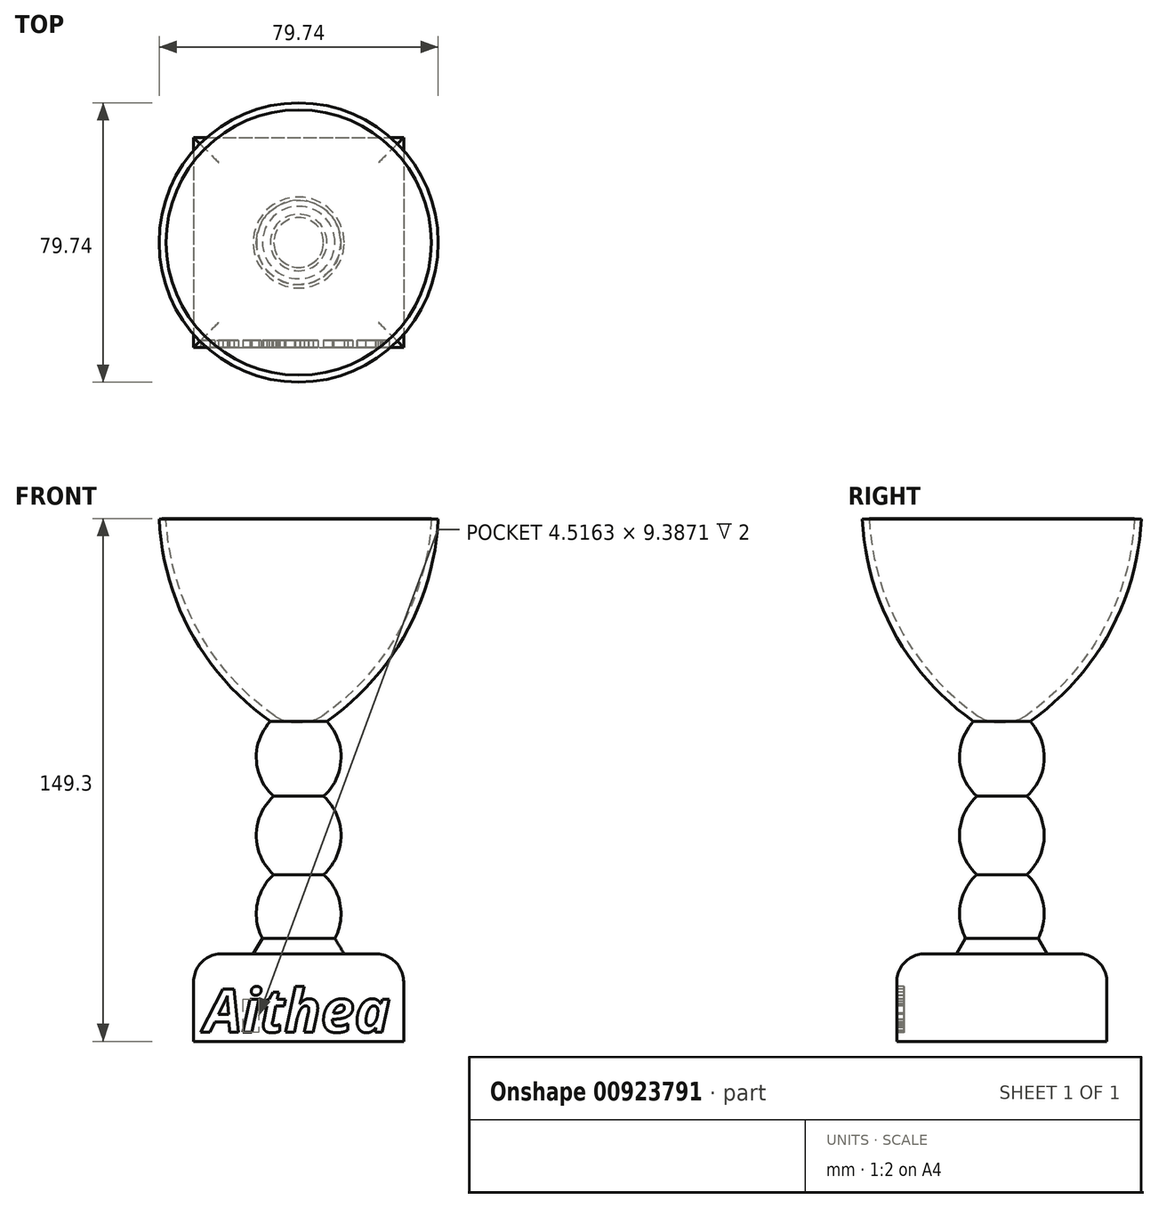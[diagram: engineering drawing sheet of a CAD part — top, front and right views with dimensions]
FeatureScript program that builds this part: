
annotation { "Feature Type Name" : "Feature", "Feature Type Description" : "" }
export const myFeature = defineFeature(function(context is Context, id is Id, definition is map)
    precondition{}
    {
        {
            var Q0;
            Q0=qCreatedBy(makeId("Top.planeOp"),FACE);
            var sketch = newSketch(context, id + "F0", { "sketchPlane" : qUnion([Q0])});
            skLineSegment(sketch, "E0.bottom", {"start": v(0, 0) * mm, "end": v(60, 0) * mm});
            skLineSegment(sketch, "E0.top", {"start": v(0, -60) * mm, "end": v(60, -60) * mm});
            skLineSegment(sketch, "E0.left", {"start": v(0, 0) * mm, "end": v(0, -60) * mm});
            skLineSegment(sketch, "E0.right", {"start": v(60, 0) * mm, "end": v(60, -60) * mm});
            skSolve(sketch);
        }
        {
            var Q0;
            Q0=makeQuery(id+"F0.imprint","IMPRINT",FACE,{"disambiguationData":[TD([[makeQuery(id+"F0.imprint","IMPRINT",EDGE,{"derivedFrom":sQuery(id+"F0.wireOp",EDGE,"E0.bottom")}),-1.0]])]});
            extrude(context, id + "F1", {"entities" : qUnion([Q0]), "depth" : 30 * mm, "offsetDistance" : 25 * mm});
        }
        {
            var Q0;
            Q0=makeQuery(id+"F1.opExtrude","SWEPT_BODY",BODY,{"disambiguationData":[OSD([sQuery(id+"F0.wireOp",EDGE,"E0.bottom"),sQuery(id+"F0.wireOp",EDGE,"E0.top"),sQuery(id+"F0.wireOp",EDGE,"E0.left"),sQuery(id+"F0.wireOp",EDGE,"E0.right")])]});
            transform(context, id + "F2", {"entities" : qUnion([Q0]), "transformType" : TransformType.TRANSLATION_3D, "dx" : -30 * mm, "dy" : 30 * mm, "dz" : 0 * mm, "makeCopy" : false});
        }
        {
            var Q0;
            Q0=qCreatedBy(makeId("Front.planeOp"),FACE);
            var sketch = newSketch(context, id + "F3", { "sketchPlane" : qUnion([Q0])});
            skArc(sketch, "E1", {"start": v(7.1, 30.27) * mm, "mid": v(12.1, 41.45) * mm, "end": v(7.1, 52.63) * mm});
            skArc(sketch, "E2", {"start": v(7.1, 52.63) * mm, "mid": v(12.1, 63.81) * mm, "end": v(7.1, 75) * mm});
            skArc(sketch, "E3", {"start": v(7.1, 75) * mm, "mid": v(12.1, 85.49) * mm, "end": v(8.09, 96.4) * mm});
            skLineSegment(sketch, "E4", {"start": v(0, 30.2) * mm, "end": v(0, 158.08) * mm});
            skLineSegment(sketch, "E5", {"start": v(7.1, 30.27) * mm, "end": v(7.1, 29.78) * mm});
            skLineSegment(sketch, "E6", {"start": v(7.1, 29.78) * mm, "end": v(0, 29.78) * mm});
            skLineSegment(sketch, "E7", {"start": v(0, 29.78) * mm, "end": v(0, 30.2) * mm});
            skArc(sketch, "E8", {"start": v(8.09, 96.4) * mm, "mid": v(30.66, 121.62) * mm, "end": v(39.87, 154.2) * mm});
            skLineSegment(sketch, "E9", {"start": v(37.87, 154.3) * mm, "end": v(39.87, 154.2) * mm});
            skLineSegment(sketch, "E10", {"start": v(0, 96.12) * mm, "end": v(1.06, 96.12) * mm});
            skArc(sketch, "E11.trimOffspring", {"start": v(6.8, 97.93) * mm, "mid": v(28.86, 122.52) * mm, "end": v(37.87, 154.3) * mm});
            skPoint(sketch, "E12.visualSharp", {"position": v(4.09, 96.12) * mm});
            skArc(sketch, "E12.filletArc", {"start": v(1.06, 96.12) * mm, "mid": v(4.07, 96.58) * mm, "end": v(6.8, 97.93) * mm});
            skLineSegment(sketch, "E13", {"start": v(0, 96.12) * mm, "end": v(11.67, 89.78) * mm});
            skSolve(sketch);
        }
        {
            var Q0;
            {var subQ10=sQuery(id+"F3.wireOp",EDGE,"I5DjJ9ts-EXyD-T3Ez-MTNL-TmspGHFE94tQ");Q0=makeQuery(id+"F3.imprint","IMPRINT",FACE,{"disambiguationData":[TD([[makeQuery(id+"F3.imprint","IMPRINT",EDGE,{"derivedFrom":subQ10}),1.0]])]});}
            var Q1;
            {var subQ0=sQuery(id+"F3.wireOp",EDGE,"E3");Q1=makeQuery(id+"F3.imprint","IMPRINT",FACE,{"disambiguationData":[TD([[makeQuery(id+"F3.imprint","IMPRINT",EDGE,{"derivedFrom":subQ0}),1.0]])]});}
            var Q2;
            {var subQ0=sQuery(id+"F3.wireOp",EDGE,"E2");Q2=makeQuery(id+"F3.imprint","IMPRINT",FACE,{"disambiguationData":[TD([[makeQuery(id+"F3.imprint","IMPRINT",EDGE,{"derivedFrom":subQ0}),1.0]])]});}
            var Q3;
            {var subQ0=sQuery(id+"F3.wireOp",EDGE,"E1");Q3=makeQuery(id+"F3.imprint","IMPRINT",FACE,{"disambiguationData":[TD([[makeQuery(id+"F3.imprint","IMPRINT",EDGE,{"derivedFrom":subQ0}),1.0]])]});}
            var Q4;
            Q4=sQuery(id+"F3.wireOp",EDGE,"E4");
            revolve(context, id + "F4", {"operationType" : NewBodyOperationType.ADD, "surfaceOperationType" : NewSurfaceOperationType.NEW, "entities" : qUnion([Q0, Q1, Q2, Q3]), "axis" : qUnion([Q4]), "revolveType" : RevolveType.FULL});
        }
        {
            var Q0;
            Q0=makeQuery(id+"F4.opRevolve","SWEPT_EDGE",EDGE,{"disambiguationData":[OSD([sQuery(id+"F3.wireOp",EDGE,"vcvWEaiL-wYzA-kxNN-2hgw-6SO7PC0KjmtI"),sQuery(id+"F3.wireOp",EDGE,"E1"),sQuery(id+"F3.wireOp",EDGE,"E5")])]});
            fillet(context, id + "F5", {"entities" : qUnion([Q0]), "radius" : 1 * mm, "tangentPropagation" : true, "allowEdgeOverflow" : false});
        }
        {
            var Q0;
            Q0=makeQuery(id+"F5.opFillet","BLEND_EDGE",EDGE,{"blendedFrom":[makeQuery(id+"F4.opRevolve","SWEPT_EDGE",EDGE,{"disambiguationData":[OSD([sQuery(id+"F3.wireOp",EDGE,"vcvWEaiL-wYzA-kxNN-2hgw-6SO7PC0KjmtI"),sQuery(id+"F3.wireOp",EDGE,"E1"),sQuery(id+"F3.wireOp",EDGE,"E5")])]}),makeQuery(id+"F1.opExtrude","CAP_FACE",FACE,{"disambiguationData":[OSD([sQuery(id+"F0.wireOp",EDGE,"E0.bottom"),sQuery(id+"F0.wireOp",EDGE,"E0.top"),sQuery(id+"F0.wireOp",EDGE,"E0.left"),sQuery(id+"F0.wireOp",EDGE,"E0.right")])],"isStart":false})],"blendedInto":[makeQuery(id+"F1.opExtrude","CAP_FACE",FACE,{"disambiguationData":[OSD([sQuery(id+"F0.wireOp",EDGE,"E0.bottom"),sQuery(id+"F0.wireOp",EDGE,"E0.top"),sQuery(id+"F0.wireOp",EDGE,"E0.left"),sQuery(id+"F0.wireOp",EDGE,"E0.right")])],"isStart":false})]});
            chamfer(context, id + "F6", {"entities" : qUnion([Q0]), "width" : 3 * mm, "tangentPropagation" : true});
        }
        {
            var Q0;
            Q0=makeQuery(id+"F1.opExtrude","CAP_EDGE",EDGE,{"disambiguationData":[OSD([sQuery(id+"F0.wireOp",EDGE,"E0.left")])],"isStart":false});
            var Q1;
            Q1=makeQuery(id+"F1.opExtrude","CAP_EDGE",EDGE,{"disambiguationData":[OSD([sQuery(id+"F0.wireOp",EDGE,"E0.bottom")])],"isStart":false});
            var Q2;
            Q2=makeQuery(id+"F1.opExtrude","CAP_EDGE",EDGE,{"disambiguationData":[OSD([sQuery(id+"F0.wireOp",EDGE,"E0.right")])],"isStart":false});
            var Q3;
            Q3=makeQuery(id+"F1.opExtrude","CAP_EDGE",EDGE,{"disambiguationData":[OSD([sQuery(id+"F0.wireOp",EDGE,"E0.top")])],"isStart":false});
            fillet(context, id + "F7", {"entities" : qUnion([Q0, Q1, Q2, Q3]), "radius" : 8 * mm, "tangentPropagation" : true, "allowEdgeOverflow" : false});
        }
        {
            var Q0;
            Q0=makeQuery(id+"F1.opExtrude","SWEPT_FACE",FACE,{"disambiguationData":[OSD([sQuery(id+"F0.wireOp",EDGE,"E0.top")])]});
            var sketch = newSketch(context, id + "F8", { "sketchPlane" : qUnion([Q0])});
            skText(sketch, "E14", { "text": "Aithea", "fontName": "OpenSans-BoldItalic.ttf"});
            const initialGuessF8  = {"E14": [-0.027, 0.00762, 1, 0, 0.01238]};
            skSetInitialGuess(sketch, initialGuessF8);
            skSolve(sketch);
        }
        {
            var Q0;
            Q0 = qSketchRegion(id + "F8", true);
            extrude(context, id + "F9", {"entities" : qUnion([Q0]), "operationType" : NewBodyOperationType.REMOVE, "oppositeDirection" : true, "depth" : 2 * mm, "offsetDistance" : 25 * mm});
        }
        {
            var Q0;
            Q0=makeQuery(id+"F1.opExtrude","CAP_FACE",FACE,{"disambiguationData":[OSD([sQuery(id+"F0.wireOp",EDGE,"E0.bottom"),sQuery(id+"F0.wireOp",EDGE,"E0.top"),sQuery(id+"F0.wireOp",EDGE,"E0.left"),sQuery(id+"F0.wireOp",EDGE,"E0.right")])],"isStart":true});
            extrude(context, id + "F10", {"entities" : qUnion([Q0]), "operationType" : NewBodyOperationType.REMOVE, "oppositeDirection" : true, "depth" : 5 * mm, "offsetDistance" : 25 * mm});
        }
    });
